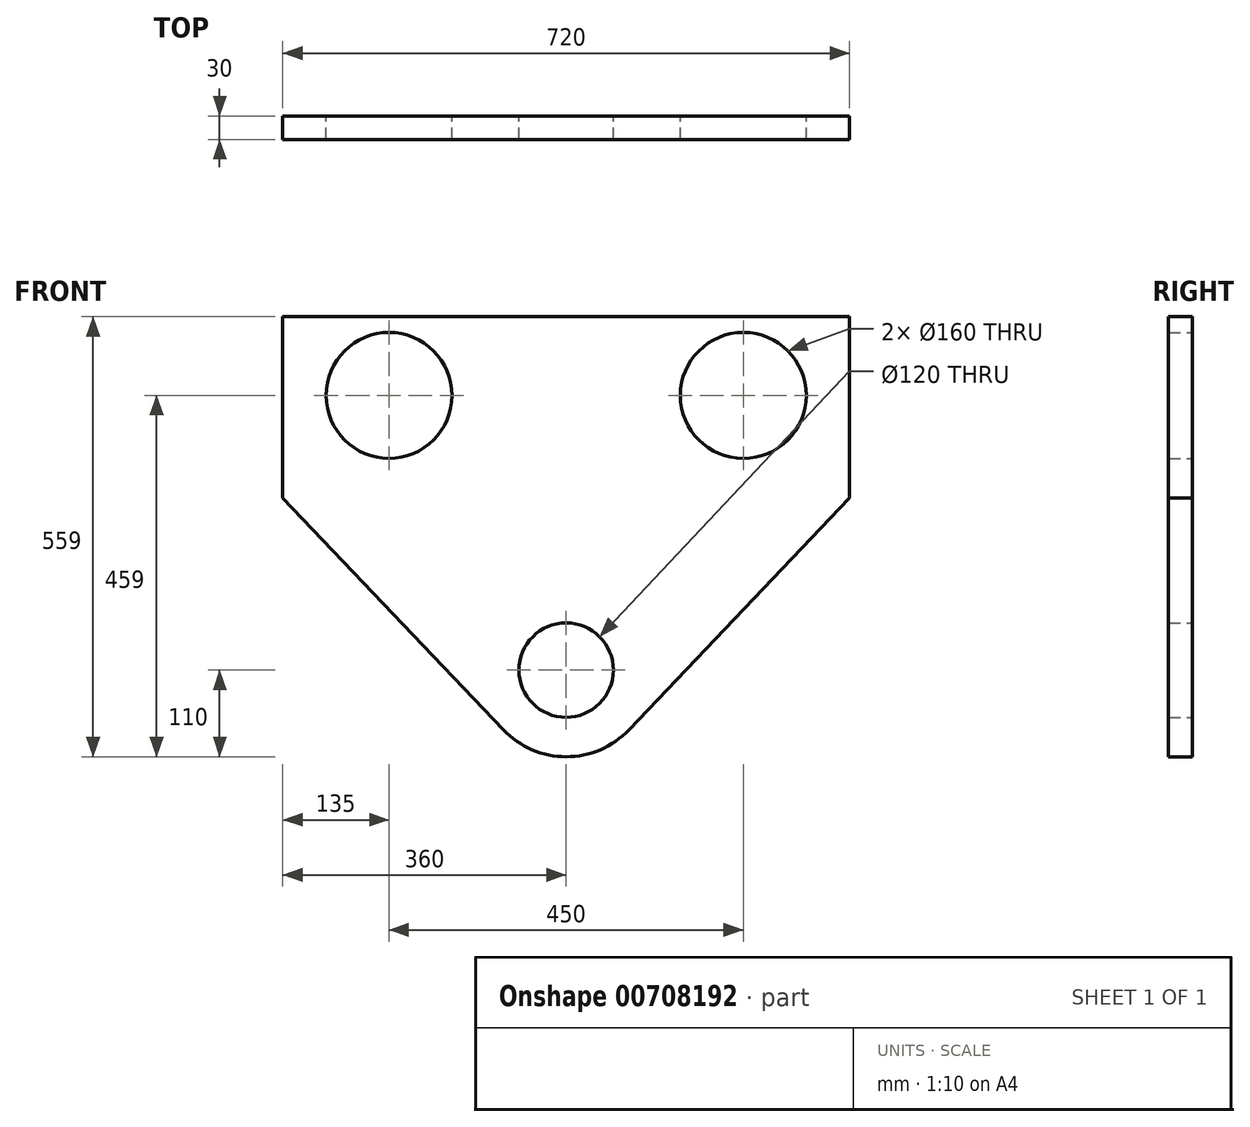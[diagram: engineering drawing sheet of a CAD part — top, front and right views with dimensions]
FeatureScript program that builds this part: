
annotation { "Feature Type Name" : "Feature", "Feature Type Description" : "" }
export const myFeature = defineFeature(function(context is Context, id is Id, definition is map)
    precondition{}
    {
        {
            var Q0;
            Q0=qCreatedBy(makeId("Front.planeOp"),FACE);
            var sketch = newSketch(context, id + "F0", { "sketchPlane" : qUnion([Q0])});
            skCircle(sketch, "E0", {"center": v(0, 0) * mm, "radius": 60 * mm});
            skCircle(sketch, "E1", {"center": v(225, 349) * mm, "radius": 80 * mm});
            skCircle(sketch, "E2", {"center": v(-225, 349) * mm, "radius": 80 * mm});
            skLineSegment(sketch, "E3", {"start": v(-360, 449) * mm, "end": v(360, 449) * mm});
            skLineSegment(sketch, "E4", {"start": v(360, 449) * mm, "end": v(360, 219) * mm});
            skLineSegment(sketch, "E5", {"start": v(360, 219) * mm, "end": v(79.72, -75.8) * mm});
            skLineSegment(sketch, "E6", {"start": v(-360, 449) * mm, "end": v(-360, 219) * mm});
            skLineSegment(sketch, "E7", {"start": v(-360, 219) * mm, "end": v(-79.72, -75.8) * mm});
            skArc(sketch, "E8", {"start": v(-79.72, -75.8) * mm, "mid": v(0, -110) * mm, "end": v(79.72, -75.8) * mm});
            skSolve(sketch);
        }
        {
            var Q0;
            Q0=makeQuery(id+"F0.imprint","IMPRINT",FACE,{"disambiguationData":[TD([[makeQuery(id+"F0.imprint","IMPRINT",EDGE,{"derivedFrom":sQuery(id+"F0.wireOp",EDGE,"E0")}),-1.0]])]});
            extrude(context, id + "F1", {"entities" : qUnion([Q0]), "endBound" : BoundingType.SYMMETRIC, "depth" : 30 * mm, "offsetDistance" : 25 * mm});
        }
    });
